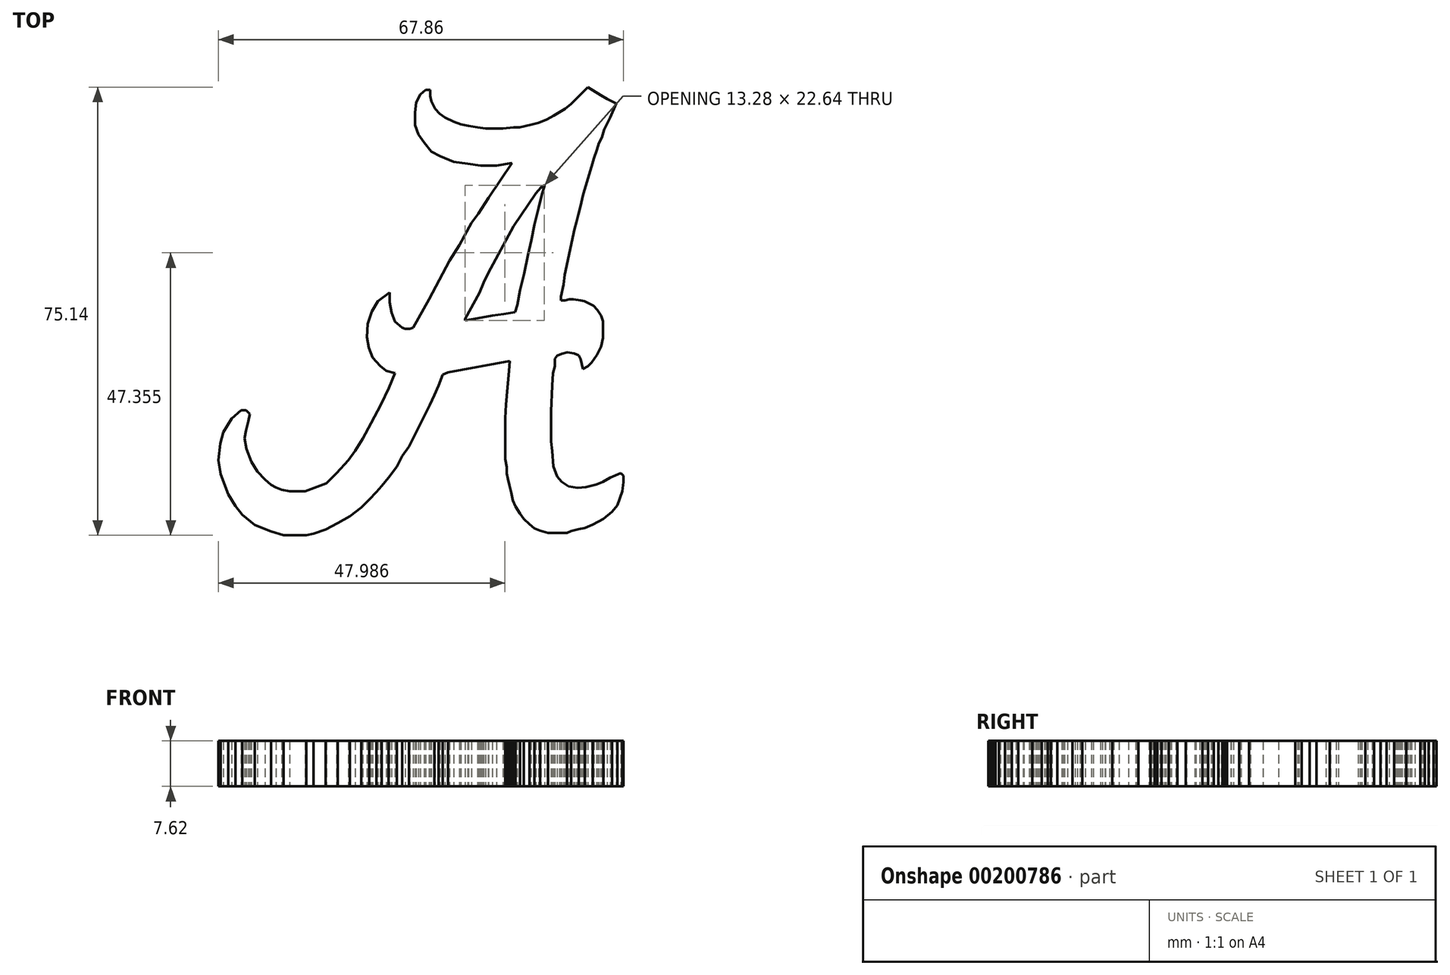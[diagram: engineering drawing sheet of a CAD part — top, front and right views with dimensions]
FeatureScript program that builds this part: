
annotation { "Feature Type Name" : "Feature", "Feature Type Description" : "" }
export const myFeature = defineFeature(function(context is Context, id is Id, definition is map)
    precondition{}
    {
        {
            var Q0;
            Q0=qCreatedBy(makeId("Top.planeOp"),FACE);
            var sketch = newSketch(context, id + "F0", { "sketchPlane" : qUnion([Q0])});
            skLineSegment(sketch, "E0", {"start": v(8.85, 38.74) * mm, "end": v(8.85, 37.68) * mm});
            skLineSegment(sketch, "E1", {"start": v(8.85, 37.68) * mm, "end": v(9.06, 36.8) * mm});
            skLineSegment(sketch, "E2", {"start": v(9.06, 36.8) * mm, "end": v(9.68, 35.53) * mm});
            skLineSegment(sketch, "E3", {"start": v(9.68, 35.53) * mm, "end": v(10.43, 34.7) * mm});
            skLineSegment(sketch, "E4", {"start": v(10.43, 34.7) * mm, "end": v(11.34, 34.06) * mm});
            skLineSegment(sketch, "E5", {"start": v(11.34, 34.06) * mm, "end": v(12.77, 33.37) * mm});
            skLineSegment(sketch, "E6", {"start": v(12.77, 33.37) * mm, "end": v(14.02, 32.97) * mm});
            skLineSegment(sketch, "E7", {"start": v(14.02, 32.97) * mm, "end": v(15.3, 32.69) * mm});
            skLineSegment(sketch, "E8", {"start": v(15.3, 32.69) * mm, "end": v(16.8, 32.43) * mm});
            skLineSegment(sketch, "E9", {"start": v(16.8, 32.43) * mm, "end": v(18.15, 32.27) * mm});
            skLineSegment(sketch, "E10", {"start": v(18.15, 32.27) * mm, "end": v(19.66, 32.27) * mm});
            skLineSegment(sketch, "E11", {"start": v(19.66, 32.27) * mm, "end": v(21.06, 32.27) * mm});
            skLineSegment(sketch, "E12", {"start": v(21.06, 32.27) * mm, "end": v(22.81, 32.45) * mm});
            skLineSegment(sketch, "E13", {"start": v(22.81, 32.45) * mm, "end": v(23.85, 32.45) * mm});
            skLineSegment(sketch, "E14", {"start": v(23.85, 32.45) * mm, "end": v(25.74, 32.9) * mm});
            skLineSegment(sketch, "E15", {"start": v(25.74, 32.9) * mm, "end": v(27, 33.18) * mm});
            skLineSegment(sketch, "E16", {"start": v(27, 33.18) * mm, "end": v(28.4, 33.78) * mm});
            skLineSegment(sketch, "E17", {"start": v(28.4, 33.78) * mm, "end": v(29.56, 34.38) * mm});
            skLineSegment(sketch, "E18", {"start": v(29.56, 34.38) * mm, "end": v(30.5, 34.95) * mm});
            skLineSegment(sketch, "E19", {"start": v(30.5, 34.95) * mm, "end": v(31.45, 35.56) * mm});
            skLineSegment(sketch, "E20", {"start": v(31.45, 35.56) * mm, "end": v(32.5, 36.36) * mm});
            skLineSegment(sketch, "E21", {"start": v(32.5, 36.36) * mm, "end": v(33.3, 37.17) * mm});
            skLineSegment(sketch, "E22", {"start": v(33.3, 37.17) * mm, "end": v(33.66, 37.54) * mm});
            skLineSegment(sketch, "E23", {"start": v(33.66, 37.54) * mm, "end": v(34.3, 38.2) * mm});
            skLineSegment(sketch, "E24", {"start": v(34.3, 38.2) * mm, "end": v(34.84, 38.74) * mm});
            skLineSegment(sketch, "E25", {"start": v(34.84, 38.74) * mm, "end": v(35.27, 39.18) * mm});
            skLineSegment(sketch, "E26", {"start": v(35.27, 39.18) * mm, "end": v(36.09, 38.65) * mm});
            skLineSegment(sketch, "E27", {"start": v(36.09, 38.65) * mm, "end": v(37.45, 37.84) * mm});
            skLineSegment(sketch, "E28", {"start": v(37.45, 37.84) * mm, "end": v(38.55, 37.17) * mm});
            skLineSegment(sketch, "E29", {"start": v(38.55, 37.17) * mm, "end": v(39.52, 36.69) * mm});
            skLineSegment(sketch, "E30", {"start": v(39.52, 36.69) * mm, "end": v(40.03, 36.44) * mm});
            skLineSegment(sketch, "E31", {"start": v(40.03, 36.44) * mm, "end": v(39, 34.06) * mm});
            skLineSegment(sketch, "E32", {"start": v(39, 34.06) * mm, "end": v(38, 32.04) * mm});
            skLineSegment(sketch, "E33", {"start": v(38, 32.04) * mm, "end": v(37.6, 30.75) * mm});
            skLineSegment(sketch, "E34", {"start": v(37.6, 30.75) * mm, "end": v(37.12, 29.77) * mm});
            skLineSegment(sketch, "E35", {"start": v(37.12, 29.77) * mm, "end": v(36.8, 28.67) * mm});
            skLineSegment(sketch, "E36", {"start": v(36.8, 28.67) * mm, "end": v(36.28, 27.21) * mm});
            skLineSegment(sketch, "E37", {"start": v(36.28, 27.21) * mm, "end": v(35.9, 25.88) * mm});
            skLineSegment(sketch, "E38", {"start": v(35.9, 25.88) * mm, "end": v(35, 22.9) * mm});
            skLineSegment(sketch, "E39", {"start": v(35, 22.9) * mm, "end": v(34.51, 21.23) * mm});
            skLineSegment(sketch, "E40", {"start": v(34.51, 21.23) * mm, "end": v(34, 19) * mm});
            skLineSegment(sketch, "E41", {"start": v(34, 19) * mm, "end": v(33.66, 17.86) * mm});
            skLineSegment(sketch, "E42", {"start": v(33.66, 17.86) * mm, "end": v(33.39, 16.56) * mm});
            skLineSegment(sketch, "E43", {"start": v(33.39, 16.56) * mm, "end": v(33.06, 15.44) * mm});
            skLineSegment(sketch, "E44", {"start": v(33.06, 15.44) * mm, "end": v(32.72, 13.84) * mm});
            skLineSegment(sketch, "E45", {"start": v(32.72, 13.84) * mm, "end": v(32.42, 12.46) * mm});
            skLineSegment(sketch, "E46", {"start": v(32.42, 12.46) * mm, "end": v(32.14, 11.13) * mm});
            skLineSegment(sketch, "E47", {"start": v(32.14, 11.13) * mm, "end": v(31.88, 9.9) * mm});
            skLineSegment(sketch, "E48", {"start": v(31.88, 9.9) * mm, "end": v(31.65, 8.78) * mm});
            skLineSegment(sketch, "E49", {"start": v(31.65, 8.78) * mm, "end": v(31.42, 7.73) * mm});
            skLineSegment(sketch, "E50", {"start": v(31.42, 7.73) * mm, "end": v(31.2, 6.07) * mm});
            skLineSegment(sketch, "E51", {"start": v(31.2, 6.07) * mm, "end": v(30.94, 4.87) * mm});
            skLineSegment(sketch, "E52", {"start": v(30.94, 4.87) * mm, "end": v(30.76, 4.03) * mm});
            skLineSegment(sketch, "E53", {"start": v(30.76, 4.03) * mm, "end": v(30.76, 3.4) * mm});
            skLineSegment(sketch, "E54", {"start": v(30.76, 3.4) * mm, "end": v(31.45, 3.4) * mm});
            skLineSegment(sketch, "E55", {"start": v(31.45, 3.4) * mm, "end": v(32.14, 3.6) * mm});
            skLineSegment(sketch, "E56", {"start": v(32.14, 3.6) * mm, "end": v(32.87, 3.6) * mm});
            skLineSegment(sketch, "E57", {"start": v(32.87, 3.6) * mm, "end": v(33.39, 3.53) * mm});
            skLineSegment(sketch, "E58", {"start": v(33.39, 3.53) * mm, "end": v(34.1, 3.43) * mm});
            skLineSegment(sketch, "E59", {"start": v(34.1, 3.43) * mm, "end": v(34.71, 3.3) * mm});
            skLineSegment(sketch, "E60", {"start": v(34.71, 3.3) * mm, "end": v(35.52, 2.9) * mm});
            skLineSegment(sketch, "E61", {"start": v(35.52, 2.9) * mm, "end": v(36.24, 2.55) * mm});
            skLineSegment(sketch, "E62", {"start": v(36.24, 2.55) * mm, "end": v(36.85, 1.8) * mm});
            skLineSegment(sketch, "E63", {"start": v(36.85, 1.8) * mm, "end": v(37.47, 0.85) * mm});
            skLineSegment(sketch, "E64", {"start": v(37.47, 0.85) * mm, "end": v(37.82, -0.1) * mm});
            skLineSegment(sketch, "E65", {"start": v(37.82, -0.1) * mm, "end": v(37.82, -1.77) * mm});
            skLineSegment(sketch, "E66", {"start": v(37.82, -1.77) * mm, "end": v(37.82, -2.9) * mm});
            skLineSegment(sketch, "E67", {"start": v(37.82, -2.9) * mm, "end": v(37.53, -4.3) * mm});
            skLineSegment(sketch, "E68", {"start": v(37.53, -4.3) * mm, "end": v(36.81, -5.75) * mm});
            skLineSegment(sketch, "E69", {"start": v(36.81, -5.75) * mm, "end": v(35.9, -6.98) * mm});
            skLineSegment(sketch, "E70", {"start": v(35.9, -6.98) * mm, "end": v(35.25, -7.63) * mm});
            skLineSegment(sketch, "E71", {"start": v(35.25, -7.63) * mm, "end": v(34.43, -8.07) * mm});
            skLineSegment(sketch, "E72", {"start": v(34.43, -8.07) * mm, "end": v(34.27, -7.26) * mm});
            skLineSegment(sketch, "E73", {"start": v(34.27, -7.26) * mm, "end": v(34.06, -6.43) * mm});
            skLineSegment(sketch, "E74", {"start": v(34.06, -6.43) * mm, "end": v(33.72, -5.82) * mm});
            skLineSegment(sketch, "E75", {"start": v(33.72, -5.82) * mm, "end": v(33, -5.46) * mm});
            skLineSegment(sketch, "E76", {"start": v(33, -5.46) * mm, "end": v(31.87, -5.3) * mm});
            skLineSegment(sketch, "E77", {"start": v(31.87, -5.3) * mm, "end": v(30.9, -5.53) * mm});
            skLineSegment(sketch, "E78", {"start": v(30.9, -5.53) * mm, "end": v(30.15, -5.86) * mm});
            skLineSegment(sketch, "E79", {"start": v(30.15, -5.86) * mm, "end": v(29.73, -6.34) * mm});
            skLineSegment(sketch, "E80", {"start": v(29.73, -6.34) * mm, "end": v(29.73, -7.64) * mm});
            skLineSegment(sketch, "E81", {"start": v(29.73, -7.64) * mm, "end": v(29.46, -8.78) * mm});
            skLineSegment(sketch, "E82", {"start": v(29.46, -8.78) * mm, "end": v(29.29, -10.84) * mm});
            skLineSegment(sketch, "E83", {"start": v(29.29, -10.84) * mm, "end": v(29.1, -15.2) * mm});
            skLineSegment(sketch, "E84", {"start": v(29.1, -15.2) * mm, "end": v(29.1, -17.94) * mm});
            skLineSegment(sketch, "E85", {"start": v(29.1, -17.94) * mm, "end": v(29.1, -20.2) * mm});
            skLineSegment(sketch, "E86", {"start": v(29.1, -20.2) * mm, "end": v(29.29, -21.87) * mm});
            skLineSegment(sketch, "E87", {"start": v(29.29, -21.87) * mm, "end": v(29.52, -24.42) * mm});
            skLineSegment(sketch, "E88", {"start": v(29.52, -24.42) * mm, "end": v(30.15, -26.08) * mm});
            skLineSegment(sketch, "E89", {"start": v(30.15, -26.08) * mm, "end": v(30.9, -26.98) * mm});
            skLineSegment(sketch, "E90", {"start": v(30.9, -26.98) * mm, "end": v(32.02, -27.75) * mm});
            skLineSegment(sketch, "E91", {"start": v(32.02, -27.75) * mm, "end": v(33.53, -28) * mm});
            skLineSegment(sketch, "E92", {"start": v(33.53, -28) * mm, "end": v(34.93, -27.87) * mm});
            skLineSegment(sketch, "E93", {"start": v(34.93, -27.87) * mm, "end": v(36.75, -27.45) * mm});
            skLineSegment(sketch, "E94", {"start": v(36.75, -27.45) * mm, "end": v(37.83, -26.98) * mm});
            skLineSegment(sketch, "E95", {"start": v(37.83, -26.98) * mm, "end": v(39, -26.3) * mm});
            skLineSegment(sketch, "E96", {"start": v(39, -26.3) * mm, "end": v(40.15, -25.8) * mm});
            skLineSegment(sketch, "E97", {"start": v(40.15, -25.8) * mm, "end": v(40.83, -25.51) * mm});
            skLineSegment(sketch, "E98", {"start": v(40.83, -25.51) * mm, "end": v(41.24, -26.02) * mm});
            skLineSegment(sketch, "E99", {"start": v(41.24, -26.02) * mm, "end": v(41.24, -27.04) * mm});
            skLineSegment(sketch, "E100", {"start": v(41.24, -27.04) * mm, "end": v(41.04, -28.6) * mm});
            skLineSegment(sketch, "E101", {"start": v(41.04, -28.6) * mm, "end": v(40.23, -30.97) * mm});
            skLineSegment(sketch, "E102", {"start": v(40.23, -30.97) * mm, "end": v(39.34, -32) * mm});
            skLineSegment(sketch, "E103", {"start": v(39.34, -32) * mm, "end": v(37.86, -33.2) * mm});
            skLineSegment(sketch, "E104", {"start": v(37.86, -33.2) * mm, "end": v(36.09, -34.16) * mm});
            skLineSegment(sketch, "E105", {"start": v(36.09, -34.16) * mm, "end": v(34.77, -34.73) * mm});
            skLineSegment(sketch, "E106", {"start": v(34.77, -34.73) * mm, "end": v(33.72, -34.93) * mm});
            skLineSegment(sketch, "E107", {"start": v(33.72, -34.93) * mm, "end": v(32.48, -35.25) * mm});
            skLineSegment(sketch, "E108", {"start": v(32.48, -35.25) * mm, "end": v(31.8, -35.55) * mm});
            skLineSegment(sketch, "E109", {"start": v(31.8, -35.55) * mm, "end": v(28.62, -35.55) * mm});
            skLineSegment(sketch, "E110", {"start": v(28.62, -35.55) * mm, "end": v(27.26, -35.2) * mm});
            skLineSegment(sketch, "E111", {"start": v(27.26, -35.2) * mm, "end": v(26.33, -34.8) * mm});
            skLineSegment(sketch, "E112", {"start": v(26.33, -34.8) * mm, "end": v(25.48, -34.14) * mm});
            skLineSegment(sketch, "E113", {"start": v(25.48, -34.14) * mm, "end": v(24.56, -33.21) * mm});
            skLineSegment(sketch, "E114", {"start": v(24.56, -33.21) * mm, "end": v(23.92, -32.3) * mm});
            skLineSegment(sketch, "E115", {"start": v(23.92, -32.3) * mm, "end": v(23.14, -31.14) * mm});
            skLineSegment(sketch, "E116", {"start": v(23.14, -31.14) * mm, "end": v(22.7, -30.1) * mm});
            skLineSegment(sketch, "E117", {"start": v(22.7, -30.1) * mm, "end": v(22.44, -28.83) * mm});
            skLineSegment(sketch, "E118", {"start": v(22.44, -28.83) * mm, "end": v(22.12, -27.6) * mm});
            skLineSegment(sketch, "E119", {"start": v(22.12, -27.6) * mm, "end": v(21.87, -26.47) * mm});
            skLineSegment(sketch, "E120", {"start": v(21.87, -26.47) * mm, "end": v(21.69, -25.64) * mm});
            skLineSegment(sketch, "E121", {"start": v(21.69, -25.64) * mm, "end": v(21.69, -24.54) * mm});
            skLineSegment(sketch, "E122", {"start": v(21.69, -24.54) * mm, "end": v(21.42, -23.22) * mm});
            skLineSegment(sketch, "E123", {"start": v(21.42, -23.22) * mm, "end": v(21.42, -21.78) * mm});
            skLineSegment(sketch, "E124", {"start": v(21.42, -21.78) * mm, "end": v(21.42, -19.76) * mm});
            skLineSegment(sketch, "E125", {"start": v(21.42, -19.76) * mm, "end": v(21.42, -17.72) * mm});
            skLineSegment(sketch, "E126", {"start": v(21.42, -17.72) * mm, "end": v(21.42, -16.36) * mm});
            skLineSegment(sketch, "E127", {"start": v(21.42, -16.36) * mm, "end": v(21.55, -14.03) * mm});
            skLineSegment(sketch, "E128", {"start": v(21.55, -14.03) * mm, "end": v(21.84, -11.16) * mm});
            skLineSegment(sketch, "E129", {"start": v(21.84, -11.16) * mm, "end": v(22.06, -8.38) * mm});
            skLineSegment(sketch, "E130", {"start": v(22.06, -8.38) * mm, "end": v(22.2, -6.76) * mm});
            skLineSegment(sketch, "E131", {"start": v(22.2, -6.76) * mm, "end": v(20.02, -7.16) * mm});
            skLineSegment(sketch, "E132", {"start": v(20.02, -7.16) * mm, "end": v(17.99, -7.53) * mm});
            skLineSegment(sketch, "E133", {"start": v(17.99, -7.53) * mm, "end": v(15.92, -7.9) * mm});
            skLineSegment(sketch, "E134", {"start": v(15.92, -7.9) * mm, "end": v(13.88, -8.28) * mm});
            skLineSegment(sketch, "E135", {"start": v(13.88, -8.28) * mm, "end": v(11.84, -8.65) * mm});
            skLineSegment(sketch, "E136", {"start": v(11.84, -8.65) * mm, "end": v(10.94, -9.04) * mm});
            skLineSegment(sketch, "E137", {"start": v(10.94, -9.04) * mm, "end": v(10.25, -10.88) * mm});
            skLineSegment(sketch, "E138", {"start": v(10.25, -10.88) * mm, "end": v(9.57, -12.48) * mm});
            skLineSegment(sketch, "E139", {"start": v(9.57, -12.48) * mm, "end": v(8.78, -14.1) * mm});
            skLineSegment(sketch, "E140", {"start": v(8.78, -14.1) * mm, "end": v(7.97, -15.73) * mm});
            skLineSegment(sketch, "E141", {"start": v(7.97, -15.73) * mm, "end": v(7.04, -17.6) * mm});
            skLineSegment(sketch, "E142", {"start": v(7.04, -17.6) * mm, "end": v(6.4, -18.89) * mm});
            skLineSegment(sketch, "E143", {"start": v(6.4, -18.89) * mm, "end": v(5.67, -20.32) * mm});
            skLineSegment(sketch, "E144", {"start": v(5.67, -20.32) * mm, "end": v(5.3, -21.07) * mm});
            skLineSegment(sketch, "E145", {"start": v(5.3, -21.07) * mm, "end": v(4.17, -22.67) * mm});
            skLineSegment(sketch, "E146", {"start": v(4.17, -22.67) * mm, "end": v(3.26, -24.5) * mm});
            skLineSegment(sketch, "E147", {"start": v(3.26, -24.5) * mm, "end": v(1.84, -26.32) * mm});
            skLineSegment(sketch, "E148", {"start": v(1.84, -26.32) * mm, "end": v(0.73, -27.7) * mm});
            skLineSegment(sketch, "E149", {"start": v(0.73, -27.7) * mm, "end": v(-0.16, -28.7) * mm});
            skLineSegment(sketch, "E150", {"start": v(-0.16, -28.7) * mm, "end": v(-1.37, -29.98) * mm});
            skLineSegment(sketch, "E151", {"start": v(-1.37, -29.98) * mm, "end": v(-2.7, -31.34) * mm});
            skLineSegment(sketch, "E152", {"start": v(-2.7, -31.34) * mm, "end": v(-4.62, -32.78) * mm});
            skLineSegment(sketch, "E153", {"start": v(-4.62, -32.78) * mm, "end": v(-6.61, -33.94) * mm});
            skLineSegment(sketch, "E154", {"start": v(-6.61, -33.94) * mm, "end": v(-8.68, -34.97) * mm});
            skLineSegment(sketch, "E155", {"start": v(-8.68, -34.97) * mm, "end": v(-10.68, -35.73) * mm});
            skLineSegment(sketch, "E156", {"start": v(-10.68, -35.73) * mm, "end": v(-11.94, -35.96) * mm});
            skLineSegment(sketch, "E157", {"start": v(-11.94, -35.96) * mm, "end": v(-15.75, -35.96) * mm});
            skLineSegment(sketch, "E158", {"start": v(-15.75, -35.96) * mm, "end": v(-17.79, -35.33) * mm});
            skLineSegment(sketch, "E159", {"start": v(-17.79, -35.33) * mm, "end": v(-20.56, -34.27) * mm});
            skLineSegment(sketch, "E160", {"start": v(-20.56, -34.27) * mm, "end": v(-22.63, -32.55) * mm});
            skLineSegment(sketch, "E161", {"start": v(-22.63, -32.55) * mm, "end": v(-23.8, -31.06) * mm});
            skLineSegment(sketch, "E162", {"start": v(-23.8, -31.06) * mm, "end": v(-25, -29.1) * mm});
            skLineSegment(sketch, "E163", {"start": v(-25, -29.1) * mm, "end": v(-25.63, -27.44) * mm});
            skLineSegment(sketch, "E164", {"start": v(-25.63, -27.44) * mm, "end": v(-26.28, -25.72) * mm});
            skLineSegment(sketch, "E165", {"start": v(-26.28, -25.72) * mm, "end": v(-26.62, -23.4) * mm});
            skLineSegment(sketch, "E166", {"start": v(-26.62, -23.4) * mm, "end": v(-26.34, -20.6) * mm});
            skLineSegment(sketch, "E167", {"start": v(-26.34, -20.6) * mm, "end": v(-25.8, -18.7) * mm});
            skLineSegment(sketch, "E168", {"start": v(-25.8, -18.7) * mm, "end": v(-24.4, -16.4) * mm});
            skLineSegment(sketch, "E169", {"start": v(-24.4, -16.4) * mm, "end": v(-22.86, -14.97) * mm});
            skLineSegment(sketch, "E170", {"start": v(-22.86, -14.97) * mm, "end": v(-21.98, -14.97) * mm});
            skLineSegment(sketch, "E171", {"start": v(-21.98, -14.97) * mm, "end": v(-21.35, -15.65) * mm});
            skLineSegment(sketch, "E172", {"start": v(-21.35, -15.65) * mm, "end": v(-21.62, -16.86) * mm});
            skLineSegment(sketch, "E173", {"start": v(-21.62, -16.86) * mm, "end": v(-22, -18.35) * mm});
            skLineSegment(sketch, "E174", {"start": v(-22, -18.35) * mm, "end": v(-22.25, -19.69) * mm});
            skLineSegment(sketch, "E175", {"start": v(-22.25, -19.69) * mm, "end": v(-21.93, -21.45) * mm});
            skLineSegment(sketch, "E176", {"start": v(-21.93, -21.45) * mm, "end": v(-21.1, -23.62) * mm});
            skLineSegment(sketch, "E177", {"start": v(-21.1, -23.62) * mm, "end": v(-20.08, -25.31) * mm});
            skLineSegment(sketch, "E178", {"start": v(-20.08, -25.31) * mm, "end": v(-18.82, -26.6) * mm});
            skLineSegment(sketch, "E179", {"start": v(-18.82, -26.6) * mm, "end": v(-17.81, -27.5) * mm});
            skLineSegment(sketch, "E180", {"start": v(-17.81, -27.5) * mm, "end": v(-17, -27.94) * mm});
            skLineSegment(sketch, "E181", {"start": v(-17, -27.94) * mm, "end": v(-16.05, -28.36) * mm});
            skLineSegment(sketch, "E182", {"start": v(-16.05, -28.36) * mm, "end": v(-14.71, -28.6) * mm});
            skLineSegment(sketch, "E183", {"start": v(-14.71, -28.6) * mm, "end": v(-13.48, -28.6) * mm});
            skLineSegment(sketch, "E184", {"start": v(-13.48, -28.6) * mm, "end": v(-12.09, -28.6) * mm});
            skLineSegment(sketch, "E185", {"start": v(-12.09, -28.6) * mm, "end": v(-10.68, -28.06) * mm});
            skLineSegment(sketch, "E186", {"start": v(-10.68, -28.06) * mm, "end": v(-8.54, -27.24) * mm});
            skLineSegment(sketch, "E187", {"start": v(-8.54, -27.24) * mm, "end": v(-6.82, -25.54) * mm});
            skLineSegment(sketch, "E188", {"start": v(-6.82, -25.54) * mm, "end": v(-4.87, -23.4) * mm});
            skLineSegment(sketch, "E189", {"start": v(-4.87, -23.4) * mm, "end": v(-3.69, -21.78) * mm});
            skLineSegment(sketch, "E190", {"start": v(-3.69, -21.78) * mm, "end": v(-2.43, -19.74) * mm});
            skLineSegment(sketch, "E191", {"start": v(-2.43, -19.74) * mm, "end": v(-1.07, -17.17) * mm});
            skLineSegment(sketch, "E192", {"start": v(-1.07, -17.17) * mm, "end": v(0.62, -14.06) * mm});
            skLineSegment(sketch, "E193", {"start": v(0.62, -14.06) * mm, "end": v(1.96, -11.26) * mm});
            skLineSegment(sketch, "E194", {"start": v(1.96, -11.26) * mm, "end": v(2.97, -8.77) * mm});
            skLineSegment(sketch, "E195", {"start": v(2.97, -8.77) * mm, "end": v(1.5, -8.39) * mm});
            skLineSegment(sketch, "E196", {"start": v(1.5, -8.39) * mm, "end": v(0.45, -7.55) * mm});
            skLineSegment(sketch, "E197", {"start": v(0.45, -7.55) * mm, "end": v(-0.81, -6.2) * mm});
            skLineSegment(sketch, "E198", {"start": v(-0.81, -6.2) * mm, "end": v(-1.44, -4.53) * mm});
            skLineSegment(sketch, "E199", {"start": v(-1.44, -4.53) * mm, "end": v(-1.77, -2.76) * mm});
            skLineSegment(sketch, "E200", {"start": v(-1.77, -2.76) * mm, "end": v(-1.6, -0.52) * mm});
            skLineSegment(sketch, "E201", {"start": v(-1.6, -0.52) * mm, "end": v(-0.91, 1.55) * mm});
            skLineSegment(sketch, "E202", {"start": v(-0.91, 1.55) * mm, "end": v(0.1, 3.32) * mm});
            skLineSegment(sketch, "E203", {"start": v(0.1, 3.32) * mm, "end": v(2.06, 4.75) * mm});
            skLineSegment(sketch, "E204", {"start": v(2.06, 4.75) * mm, "end": v(2.06, 3.11) * mm});
            skLineSegment(sketch, "E205", {"start": v(2.06, 3.11) * mm, "end": v(2.4, 1.37) * mm});
            skLineSegment(sketch, "E206", {"start": v(2.4, 1.37) * mm, "end": v(2.96, -0.11) * mm});
            skLineSegment(sketch, "E207", {"start": v(2.96, -0.11) * mm, "end": v(4.13, -1.15) * mm});
            skLineSegment(sketch, "E208", {"start": v(5.97, -1.15) * mm, "end": v(8.65, 3.62) * mm});
            skLineSegment(sketch, "E209", {"start": v(8.65, 3.62) * mm, "end": v(10.1, 6.34) * mm});
            skLineSegment(sketch, "E210", {"start": v(10.1, 6.34) * mm, "end": v(12.13, 10.1) * mm});
            skLineSegment(sketch, "E211", {"start": v(12.13, 10.1) * mm, "end": v(13.77, 12.67) * mm});
            skLineSegment(sketch, "E212", {"start": v(13.77, 12.67) * mm, "end": v(14.7, 14.4) * mm});
            skLineSegment(sketch, "E213", {"start": v(14.7, 14.4) * mm, "end": v(15.79, 16.44) * mm});
            skLineSegment(sketch, "E214", {"start": v(15.79, 16.44) * mm, "end": v(16.94, 17.97) * mm});
            skLineSegment(sketch, "E215", {"start": v(16.94, 17.97) * mm, "end": v(18.63, 20.62) * mm});
            skLineSegment(sketch, "E216", {"start": v(18.63, 20.62) * mm, "end": v(20.05, 22.71) * mm});
            skLineSegment(sketch, "E217", {"start": v(20.05, 22.71) * mm, "end": v(21.27, 24.53) * mm});
            skLineSegment(sketch, "E218", {"start": v(21.27, 24.53) * mm, "end": v(22.57, 26.45) * mm});
            skLineSegment(sketch, "E219", {"start": v(22.57, 26.45) * mm, "end": v(19.97, 26.02) * mm});
            skLineSegment(sketch, "E220", {"start": v(19.97, 26.02) * mm, "end": v(17.32, 26.02) * mm});
            skLineSegment(sketch, "E221", {"start": v(17.32, 26.02) * mm, "end": v(15.15, 26.32) * mm});
            skLineSegment(sketch, "E222", {"start": v(15.15, 26.32) * mm, "end": v(12.8, 26.62) * mm});
            skLineSegment(sketch, "E223", {"start": v(12.8, 26.62) * mm, "end": v(10.54, 27.58) * mm});
            skLineSegment(sketch, "E224", {"start": v(10.54, 27.58) * mm, "end": v(9.05, 28.38) * mm});
            skLineSegment(sketch, "E225", {"start": v(9.05, 28.38) * mm, "end": v(7.86, 29.88) * mm});
            skLineSegment(sketch, "E226", {"start": v(7.86, 29.88) * mm, "end": v(6.9, 31.24) * mm});
            skLineSegment(sketch, "E227", {"start": v(6.9, 31.24) * mm, "end": v(6.3, 32.83) * mm});
            skLineSegment(sketch, "E228", {"start": v(6.3, 32.83) * mm, "end": v(6.3, 34.9) * mm});
            skLineSegment(sketch, "E229", {"start": v(6.3, 34.9) * mm, "end": v(6.5, 36.61) * mm});
            skLineSegment(sketch, "E230", {"start": v(6.5, 36.61) * mm, "end": v(7.23, 37.97) * mm});
            skLineSegment(sketch, "E231", {"start": v(7.23, 37.97) * mm, "end": v(8.07, 38.7) * mm});
            skLineSegment(sketch, "E232", {"start": v(8.07, 38.7) * mm, "end": v(8.85, 38.74) * mm});
            skLineSegment(sketch, "E233", {"start": v(28, 22.71) * mm, "end": v(27.56, 21) * mm});
            skLineSegment(sketch, "E234", {"start": v(27.56, 21) * mm, "end": v(27, 18.93) * mm});
            skLineSegment(sketch, "E235", {"start": v(27, 18.93) * mm, "end": v(26.32, 16.12) * mm});
            skLineSegment(sketch, "E236", {"start": v(26.32, 16.12) * mm, "end": v(25.78, 13.51) * mm});
            skLineSegment(sketch, "E237", {"start": v(25.78, 13.51) * mm, "end": v(25.27, 11.04) * mm});
            skLineSegment(sketch, "E238", {"start": v(25.27, 11.04) * mm, "end": v(24.64, 7.9) * mm});
            skLineSegment(sketch, "E239", {"start": v(24.64, 7.9) * mm, "end": v(23.9, 5.13) * mm});
            skLineSegment(sketch, "E240", {"start": v(23.9, 5.13) * mm, "end": v(23.45, 2.68) * mm});
            skLineSegment(sketch, "E241", {"start": v(23.45, 2.68) * mm, "end": v(23.1, 1.42) * mm});
            skLineSegment(sketch, "E242", {"start": v(23.1, 1.42) * mm, "end": v(21.18, 1.15) * mm});
            skLineSegment(sketch, "E243", {"start": v(21.18, 1.15) * mm, "end": v(19.29, 0.9) * mm});
            skLineSegment(sketch, "E244", {"start": v(19.29, 0.9) * mm, "end": v(17.56, 0.54) * mm});
            skLineSegment(sketch, "E245", {"start": v(17.56, 0.54) * mm, "end": v(15.92, 0.27) * mm});
            skLineSegment(sketch, "E246", {"start": v(14.73, 0.27) * mm, "end": v(16.14, 2.91) * mm});
            skLineSegment(sketch, "E247", {"start": v(16.14, 2.91) * mm, "end": v(17.09, 4.68) * mm});
            skLineSegment(sketch, "E248", {"start": v(18.6, 7.96) * mm, "end": v(20.27, 11.08) * mm});
            skLineSegment(sketch, "E249", {"start": v(20.27, 11.08) * mm, "end": v(21.07, 12.57) * mm});
            skLineSegment(sketch, "E250", {"start": v(21.07, 12.57) * mm, "end": v(21.9, 14.11) * mm});
            skLineSegment(sketch, "E251", {"start": v(21.9, 14.11) * mm, "end": v(22.84, 15.86) * mm});
            skLineSegment(sketch, "E252", {"start": v(22.84, 15.86) * mm, "end": v(23.71, 17.17) * mm});
            skLineSegment(sketch, "E253", {"start": v(23.71, 17.17) * mm, "end": v(24.53, 18.37) * mm});
            skLineSegment(sketch, "E254", {"start": v(24.53, 18.37) * mm, "end": v(25.64, 20.02) * mm});
            skLineSegment(sketch, "E255", {"start": v(25.64, 20.02) * mm, "end": v(26.55, 21.36) * mm});
            skLineSegment(sketch, "E256", {"start": v(26.55, 21.36) * mm, "end": v(27.4, 22.34) * mm});
            skLineSegment(sketch, "E257", {"start": v(27.4, 22.34) * mm, "end": v(28, 22.71) * mm});
            skLineSegment(sketch, "E258", {"start": v(15.92, 0.27) * mm, "end": v(15.19, 0.15) * mm});
            skLineSegment(sketch, "E259", {"start": v(15.19, 0.15) * mm, "end": v(14.72, 0.08) * mm});
            skLineSegment(sketch, "E260", {"start": v(14.72, 0.08) * mm, "end": v(14.73, 0.27) * mm});
            skLineSegment(sketch, "E261", {"start": v(4.13, -1.15) * mm, "end": v(4.7, -1.37) * mm});
            skLineSegment(sketch, "E262", {"start": v(4.7, -1.37) * mm, "end": v(5.44, -1.37) * mm});
            skLineSegment(sketch, "E263", {"start": v(5.44, -1.37) * mm, "end": v(5.97, -1.15) * mm});
            skLineSegment(sketch, "E264", {"start": v(17.09, 4.68) * mm, "end": v(17.8, 6.4) * mm});
            skLineSegment(sketch, "E265", {"start": v(17.8, 6.4) * mm, "end": v(18.6, 7.96) * mm});
            skSolve(sketch);
        }
        {
            var Q0;
            Q0=makeQuery(id+"F0.imprint","IMPRINT",FACE,{"disambiguationData":[TD([[makeQuery(id+"F0.imprint","IMPRINT",EDGE,{"derivedFrom":sQuery(id+"F0.wireOp",EDGE,"E0")}),-1.0]])]});
            var Q1;
            Q1=makeQuery(id+"F0.imprint","IMPRINT",FACE,{"disambiguationData":[TD([[makeQuery(id+"F0.imprint","IMPRINT",EDGE,{"derivedFrom":sQuery(id+"F0.wireOp",EDGE,"E233")}),-1.0]])]});
            extrude(context, id + "F1", {"entities" : qUnion([Q0, Q1]), "depth" : 7.62 * mm});
        }
        {
            var Q0;
            Q0=makeQuery(id+"F0.imprint","IMPRINT",FACE,{"disambiguationData":[TD([[makeQuery(id+"F0.imprint","IMPRINT",EDGE,{"derivedFrom":sQuery(id+"F0.wireOp",EDGE,"E233")}),-1.0]])]});
            extrude(context, id + "F2", {"entities" : qUnion([Q0]), "operationType" : NewBodyOperationType.REMOVE, "depth" : 28.2 * mm});
        }
    });
